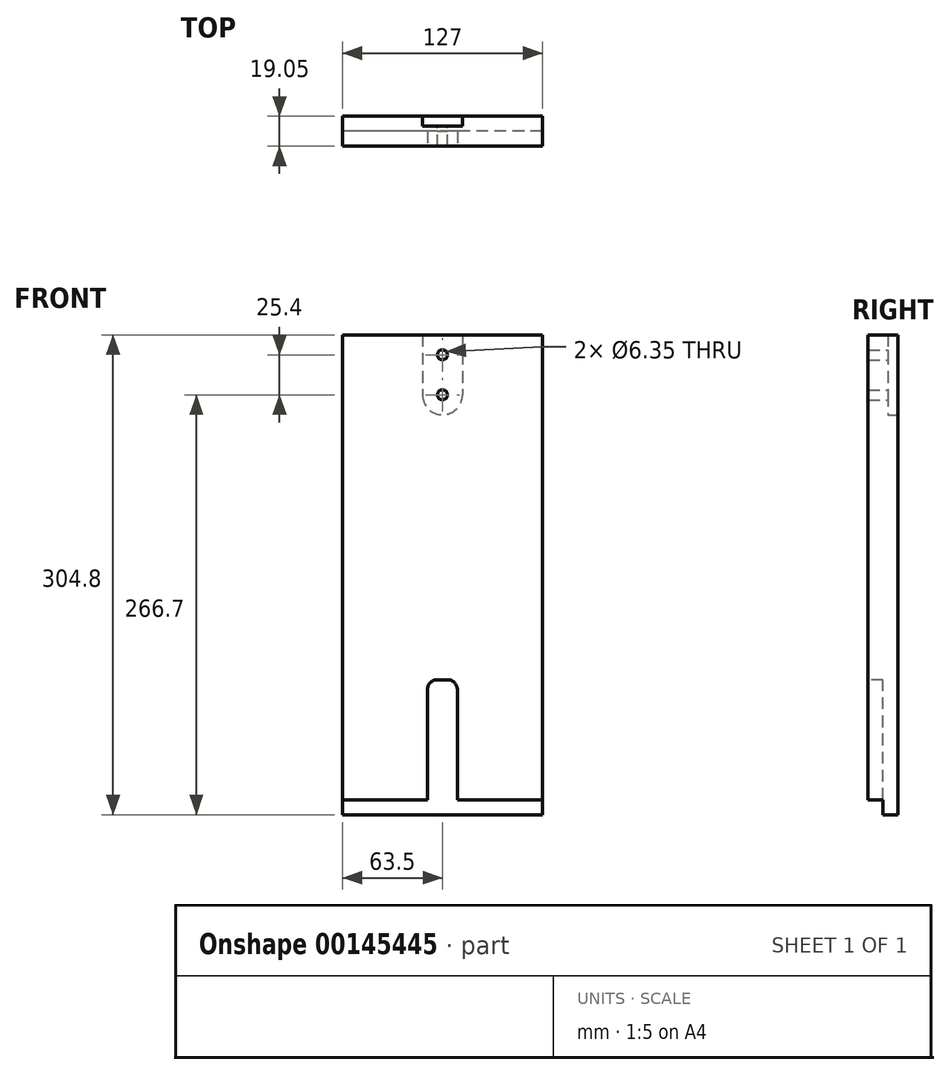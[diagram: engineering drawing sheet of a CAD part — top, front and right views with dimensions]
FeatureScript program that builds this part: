
annotation { "Feature Type Name" : "Feature", "Feature Type Description" : "" }
export const myFeature = defineFeature(function(context is Context, id is Id, definition is map)
    precondition{}
    {
        {
            var Q0;
            Q0=qCreatedBy(makeId("Front.planeOp"),FACE);
            var sketch = newSketch(context, id + "F0", { "sketchPlane" : qUnion([Q0])});
            skLineSegment(sketch, "E0.bottom", {"start": v(-63.5, 152.4) * mm, "end": v(63.5, 152.4) * mm});
            skLineSegment(sketch, "E0.top", {"start": v(-63.5, -152.4) * mm, "end": v(63.5, -152.4) * mm});
            skLineSegment(sketch, "E0.left", {"start": v(-63.5, 152.4) * mm, "end": v(-63.5, -152.4) * mm});
            skLineSegment(sketch, "E0.right", {"start": v(63.5, 152.4) * mm, "end": v(63.5, -152.4) * mm});
            skPoint(sketch, "E0.middle", {"position": v(0, 0) * mm});
            skCircle(sketch, "E1", {"center": v(0, 177.8) * mm, "radius": 279.4 * mm, "construction": true});
            skPoint(sketch, "E1.centerSnap0", {"position": v(0, 152.4) * mm});
            skSolve(sketch);
        }
        {
            var Q0;
            Q0 = qSketchRegion(id + "F0", true);
            extrude(context, id + "F1", {"entities" : qUnion([Q0]), "depth" : 19.05 * mm});
        }
        {
            var Q0;
            Q0=makeQuery(id+"F1.opExtrude","CAP_FACE",FACE,{"disambiguationData":[OSD([sQuery(id+"F0.wireOp",EDGE,"E0.bottom"),sQuery(id+"F0.wireOp",EDGE,"E0.top"),sQuery(id+"F0.wireOp",EDGE,"E0.left"),sQuery(id+"F0.wireOp",EDGE,"E0.right")])],"isStart":true});
            var sketch = newSketch(context, id + "F2", { "sketchPlane" : qUnion([Q0])});
            skArc(sketch, "E2", {"start": v(12.7, 152.4) * mm, "mid": v(0, 165.1) * mm, "end": v(-12.7, 152.4) * mm});
            skArc(sketch, "E3", {"start": v(-12.7, 114.3) * mm, "mid": v(0, 101.6) * mm, "end": v(12.7, 114.3) * mm});
            skLineSegment(sketch, "E4", {"start": v(-12.7, 152.4) * mm, "end": v(-12.7, 114.3) * mm});
            skLineSegment(sketch, "E5", {"start": v(12.7, 152.4) * mm, "end": v(12.7, 114.3) * mm});
            skSolve(sketch);
        }
        {
            var Q0;
            Q0 = qSketchRegion(id + "F2", true);
            extrude(context, id + "F3", {"entities" : qUnion([Q0]), "operationType" : NewBodyOperationType.REMOVE, "oppositeDirection" : true, "depth" : 6.35 * mm});
        }
        {
            var Q0;
            Q0=makeQuery(id+"F3.boolean.opBoolean","COPY",FACE,{"derivedFrom":makeQuery(id+"F3.opExtrude","CAP_FACE",FACE,{"disambiguationData":[OSD([sQuery(id+"F2.wireOp",EDGE,"E2"),sQuery(id+"F2.wireOp",EDGE,"E3"),sQuery(id+"F2.wireOp",EDGE,"E4"),sQuery(id+"F2.wireOp",EDGE,"E5")])],"isStart":false})});
            var sketch = newSketch(context, id + "F4", { "sketchPlane" : qUnion([Q0])});
            skCircle(sketch, "E6", {"center": v(0, 114.3) * mm, "radius": 3.18 * mm});
            skCircle(sketch, "E7", {"center": v(0, 139.7) * mm, "radius": 3.18 * mm});
            skSolve(sketch);
        }
        {
            var Q0;
            Q0 = qSketchRegion(id + "F4", true);
            extrude(context, id + "F5", {"entities" : qUnion([Q0]), "operationType" : NewBodyOperationType.REMOVE, "endBound" : BoundingType.THROUGH_ALL, "oppositeDirection" : true, "depth" : 25.4 * mm});
        }
        {
            var Q0;
            Q0=makeQuery(id+"F1.opExtrude","SWEPT_FACE",FACE,{"disambiguationData":[OSD([sQuery(id+"F0.wireOp",EDGE,"E0.left")])]});
            var sketch = newSketch(context, id + "F6", { "sketchPlane" : qUnion([Q0])});
            skLineSegment(sketch, "E8.bottom", {"start": v(9.53, -152.4) * mm, "end": v(34.93, -152.4) * mm});
            skLineSegment(sketch, "E8.top", {"start": v(9.53, -142.87) * mm, "end": v(34.93, -142.87) * mm});
            skLineSegment(sketch, "E8.left", {"start": v(9.53, -152.4) * mm, "end": v(9.53, -142.87) * mm});
            skLineSegment(sketch, "E8.right", {"start": v(34.93, -152.4) * mm, "end": v(34.93, -142.87) * mm});
            skSolve(sketch);
        }
        {
            var Q0;
            Q0 = qSketchRegion(id + "F6", true);
            extrude(context, id + "F7", {"entities" : qUnion([Q0]), "operationType" : NewBodyOperationType.REMOVE, "endBound" : BoundingType.THROUGH_ALL, "oppositeDirection" : true, "depth" : 25.4 * mm});
        }
        {
            var Q0;
            Q0=makeQuery(id+"F1.opExtrude","CAP_FACE",FACE,{"disambiguationData":[OSD([sQuery(id+"F0.wireOp",EDGE,"E0.bottom"),sQuery(id+"F0.wireOp",EDGE,"E0.top"),sQuery(id+"F0.wireOp",EDGE,"E0.left"),sQuery(id+"F0.wireOp",EDGE,"E0.right")])],"isStart":false});
            var sketch = newSketch(context, id + "F8", { "sketchPlane" : qUnion([Q0])});
            skLineSegment(sketch, "E9.bottom", {"start": v(-9.53, -142.87) * mm, "end": v(9.53, -142.87) * mm});
            skLineSegment(sketch, "E9.top", {"start": v(-9.52, -66.67) * mm, "end": v(9.52, -66.67) * mm});
            skLineSegment(sketch, "E9.left", {"start": v(-9.53, -142.87) * mm, "end": v(-9.52, -66.67) * mm});
            skLineSegment(sketch, "E9.right", {"start": v(9.52, -142.87) * mm, "end": v(9.53, -66.67) * mm});
            skLineSegment(sketch, "E10", {"start": v(0, -66.67) * mm, "end": v(0, -142.87) * mm, "construction": true});
            skPoint(sketch, "E11", {"position": v(0, -142.87) * mm});
            skSolve(sketch);
        }
        {
            var Q0;
            Q0 = qSketchRegion(id + "F8", true);
            extrude(context, id + "F9", {"entities" : qUnion([Q0]), "operationType" : NewBodyOperationType.REMOVE, "oppositeDirection" : true, "depth" : 9.52 * mm});
        }
        {
            var Q0;
            Q0=makeQuery(id+"F9.boolean.opBoolean","COPY",EDGE,{"derivedFrom":makeQuery(id+"F9.opExtrude","SWEPT_EDGE",EDGE,{"disambiguationData":[OSD([sQuery(id+"F8.wireOp",EDGE,"E9.top"),sQuery(id+"F8.wireOp",EDGE,"E9.left")])]})});
            var Q1;
            Q1=makeQuery(id+"F9.boolean.opBoolean","COPY",EDGE,{"derivedFrom":makeQuery(id+"F9.opExtrude","SWEPT_EDGE",EDGE,{"disambiguationData":[OSD([sQuery(id+"F8.wireOp",EDGE,"E9.top"),sQuery(id+"F8.wireOp",EDGE,"E9.right")])]})});
            fillet(context, id + "F10", {"entities" : qUnion([Q0, Q1]), "radius" : 6.35 * mm, "tangentPropagation" : true, "allowEdgeOverflow" : false});
        }
        {
            var Q0;
            Q0=makeQuery(id+"F1.opExtrude","SWEPT_BODY",BODY,{"disambiguationData":[OSD([sQuery(id+"F0.wireOp",EDGE,"E0.bottom"),sQuery(id+"F0.wireOp",EDGE,"E0.top"),sQuery(id+"F0.wireOp",EDGE,"E0.left"),sQuery(id+"F0.wireOp",EDGE,"E0.right")])]});
            transform(context, id + "F11", {"entities" : qUnion([Q0]), "transformType" : TransformType.COPY});
        }
        {
            var Q0;
            Q0=makeQuery(id+"F11.opPattern","COPY",BODY,{"derivedFrom":makeQuery(id+"F1.opExtrude","SWEPT_BODY",BODY,{"disambiguationData":[OSD([sQuery(id+"F0.wireOp",EDGE,"E0.bottom"),sQuery(id+"F0.wireOp",EDGE,"E0.top"),sQuery(id+"F0.wireOp",EDGE,"E0.left"),sQuery(id+"F0.wireOp",EDGE,"E0.right")])]}),"instanceName":"1"});
            deleteBodies(context, id + "F12", {"entities" : qUnion([Q0])});
        }
    });
